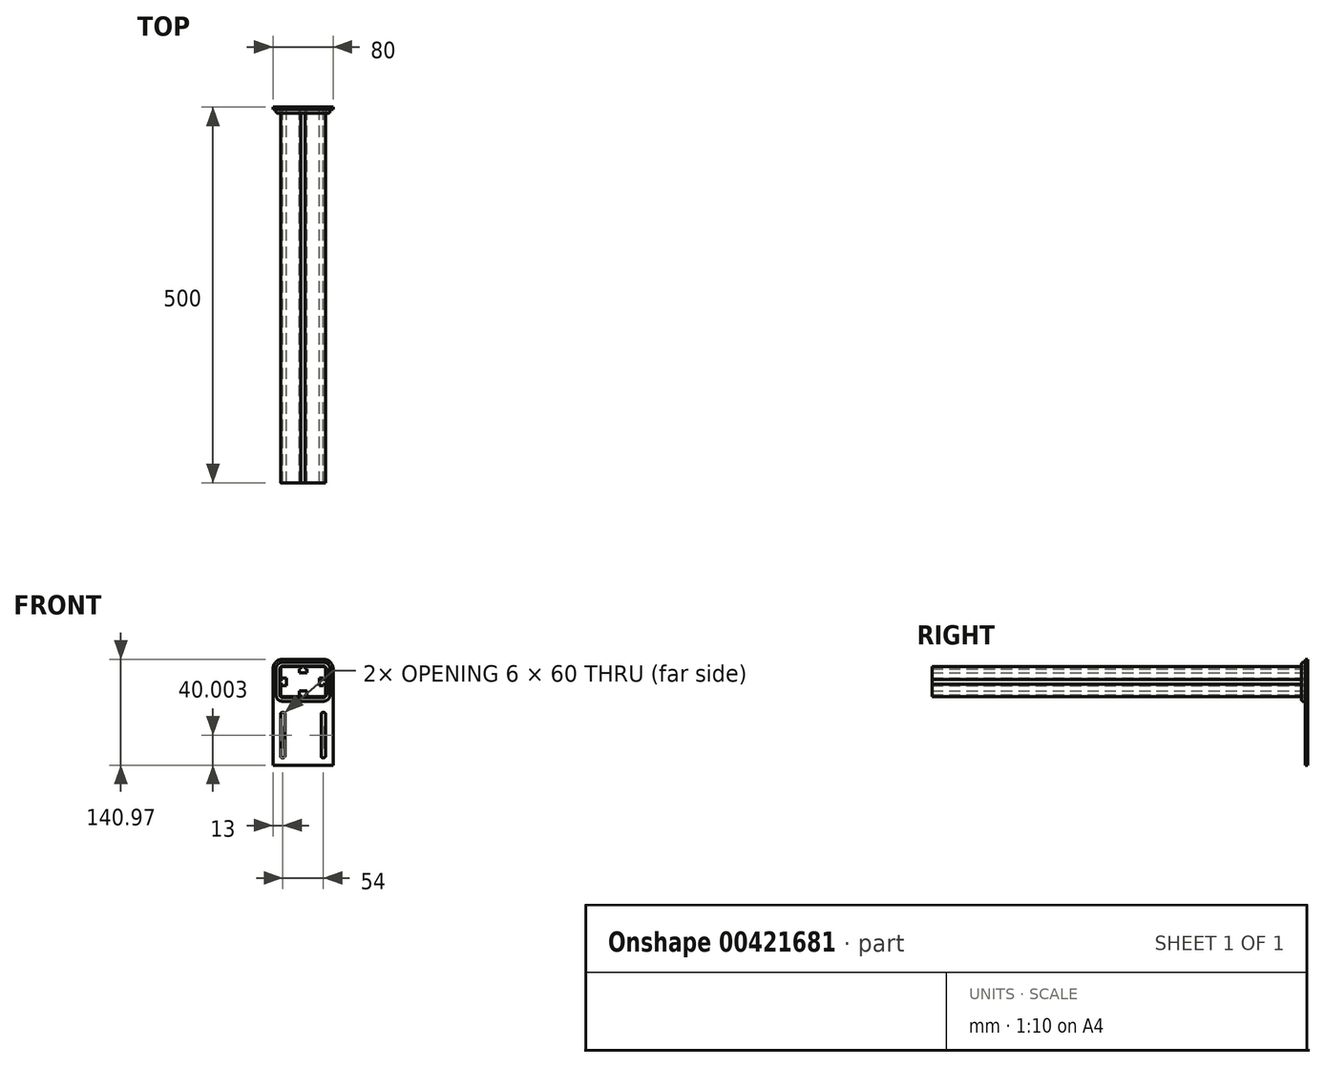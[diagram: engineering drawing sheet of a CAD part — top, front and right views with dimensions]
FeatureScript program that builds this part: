
annotation { "Feature Type Name" : "Feature", "Feature Type Description" : "" }
export const myFeature = defineFeature(function(context is Context, id is Id, definition is map)
    precondition{}
    {
        {
            var Q0;
            Q0=qCreatedBy(makeId("Front.planeOp"),FACE);
            var sketch = newSketch(context, id + "F0", { "sketchPlane" : qUnion([Q0])});
            skLineSegment(sketch, "E0.bottom", {"start": v(27, -20) * mm, "end": v(3, -20) * mm});
            skLineSegment(sketch, "E0.top", {"start": v(27, 20) * mm, "end": v(3, 20) * mm});
            skLineSegment(sketch, "E0.left", {"start": v(30, -17) * mm, "end": v(30, -3) * mm});
            skLineSegment(sketch, "E0.right", {"start": v(-30, -17) * mm, "end": v(-30, -3) * mm});
            skPoint(sketch, "E0.middle", {"position": v(0, 0) * mm});
            skPoint(sketch, "E1.visualSharp", {"position": v(-30, 20) * mm});
            skArc(sketch, "E1.filletArc", {"start": v(-27, 20) * mm, "mid": v(-29.12, 19.12) * mm, "end": v(-30, 17) * mm});
            skPoint(sketch, "E2.visualSharp", {"position": v(-30, -20) * mm});
            skArc(sketch, "E2.filletArc", {"start": v(-30, -17) * mm, "mid": v(-29.12, -19.12) * mm, "end": v(-27, -20) * mm});
            skPoint(sketch, "E3.visualSharp", {"position": v(30, -20) * mm});
            skArc(sketch, "E3.filletArc", {"start": v(27, -20) * mm, "mid": v(29.12, -19.12) * mm, "end": v(30, -17) * mm});
            skPoint(sketch, "E4.visualSharp", {"position": v(30, 20) * mm});
            skArc(sketch, "E4.filletArc", {"start": v(30, 17) * mm, "mid": v(29.12, 19.12) * mm, "end": v(27, 20) * mm});
            skLineSegment(sketch, "E5.bottom", {"start": v(5, 12) * mm, "end": v(-5, 12) * mm});
            skLineSegment(sketch, "E5.top", {"start": v(5, 17) * mm, "end": v(3, 17) * mm});
            skLineSegment(sketch, "E5.left", {"start": v(5, 12) * mm, "end": v(5, 17) * mm});
            skLineSegment(sketch, "E5.right", {"start": v(-5, 12) * mm, "end": v(-5, 17) * mm});
            skPoint(sketch, "E5.middle", {"position": v(0, 14.5) * mm});
            skLineSegment(sketch, "E6", {"start": v(-3, 17) * mm, "end": v(-3, 20) * mm});
            skLineSegment(sketch, "E7.MirrorCS", {"start": v(3, 17) * mm, "end": v(3, 20) * mm});
            skLineSegment(sketch, "E8.trimOffspring", {"start": v(-3, 20) * mm, "end": v(-27, 20) * mm});
            skLineSegment(sketch, "E9.trimOffspring", {"start": v(-3, 17) * mm, "end": v(-5, 17) * mm});
            skLineSegment(sketch, "E10.MirrorCS", {"start": v(-5, -12) * mm, "end": v(-5, -17) * mm});
            skLineSegment(sketch, "E11.MirrorCS", {"start": v(-3, -17) * mm, "end": v(-3, -20) * mm});
            skLineSegment(sketch, "E12.MirrorCS", {"start": v(3, -17) * mm, "end": v(3, -20) * mm});
            skLineSegment(sketch, "E13.MirrorCS", {"start": v(5, -12) * mm, "end": v(5, -17) * mm});
            skLineSegment(sketch, "E14.MirrorCS", {"start": v(5, -17) * mm, "end": v(3, -17) * mm});
            skLineSegment(sketch, "E15.MirrorCS", {"start": v(-3, -17) * mm, "end": v(-5, -17) * mm});
            skLineSegment(sketch, "E16.MirrorCS", {"start": v(5, -12) * mm, "end": v(-5, -12) * mm});
            skLineSegment(sketch, "E17.trimOffspring", {"start": v(-3, -20) * mm, "end": v(-27, -20) * mm});
            skLineSegment(sketch, "E18.bottom", {"start": v(-22, -5) * mm, "end": v(-27, -5) * mm});
            skLineSegment(sketch, "E18.top", {"start": v(-22, 5) * mm, "end": v(-27, 5) * mm});
            skLineSegment(sketch, "E18.left", {"start": v(-22, -5) * mm, "end": v(-22, 5) * mm});
            skLineSegment(sketch, "E18.right", {"start": v(-27, -5) * mm, "end": v(-27, -3) * mm});
            skPoint(sketch, "E18.middle", {"position": v(-24.5, 0) * mm});
            skLineSegment(sketch, "E19", {"start": v(-27, -3) * mm, "end": v(-30, -3) * mm});
            skLineSegment(sketch, "E20.MirrorCS", {"start": v(-27, 3) * mm, "end": v(-30, 3) * mm});
            skLineSegment(sketch, "E21.trimOffspring", {"start": v(-30, 3) * mm, "end": v(-30, 17) * mm});
            skLineSegment(sketch, "E22.trimOffspring", {"start": v(-27, 3) * mm, "end": v(-27, 5) * mm});
            skLineSegment(sketch, "E23.MirrorCS", {"start": v(22, 5) * mm, "end": v(27, 5) * mm});
            skLineSegment(sketch, "E24.MirrorCS", {"start": v(22, -5) * mm, "end": v(22, 5) * mm});
            skLineSegment(sketch, "E25.MirrorCS", {"start": v(22, -5) * mm, "end": v(27, -5) * mm});
            skLineSegment(sketch, "E26.MirrorCS", {"start": v(27, -3) * mm, "end": v(30, -3) * mm});
            skLineSegment(sketch, "E27.MirrorCS", {"start": v(27, 3) * mm, "end": v(30, 3) * mm});
            skLineSegment(sketch, "E28.MirrorCS", {"start": v(27, 3) * mm, "end": v(27, 5) * mm});
            skLineSegment(sketch, "E29.MirrorCS", {"start": v(27, -5) * mm, "end": v(27, -3) * mm});
            skLineSegment(sketch, "E30.trimOffspring", {"start": v(30, 3) * mm, "end": v(30, 17) * mm});
            skSolve(sketch);
        }
        {
            var Q0;
            Q0=makeQuery(id+"F0.imprint","IMPRINT",FACE,{"disambiguationData":[TD([[makeQuery(id+"F0.imprint","IMPRINT",EDGE,{"derivedFrom":sQuery(id+"F0.wireOp",EDGE,"E0.bottom")}),-1.0]])]});
            extrude(context, id + "F1", {"entities" : qUnion([Q0]), "depth" : 500 * mm, "offsetDistance" : 25 * mm});
        }
        {
            var Q0;
            Q0=qCreatedBy(makeId("Front.planeOp"),FACE);
            var sketch = newSketch(context, id + "F2", { "sketchPlane" : qUnion([Q0])});
            skLineSegment(sketch, "E31.0", {"start": v(-3, 30) * mm, "end": v(-27, 30) * mm});
            skArc(sketch, "E31.1", {"start": v(-27, 30) * mm, "mid": v(-36.2, 26.2) * mm, "end": v(-40, 17) * mm});
            skLineSegment(sketch, "E31.2", {"start": v(-40, 3) * mm, "end": v(-40, 17) * mm});
            skLineSegment(sketch, "E32.0", {"start": v(27, 30) * mm, "end": v(3, 30) * mm});
            skArc(sketch, "E32.1", {"start": v(40, 17) * mm, "mid": v(36.2, 26.2) * mm, "end": v(27, 30) * mm});
            skLineSegment(sketch, "E32.2", {"start": v(40, 3) * mm, "end": v(40, 17) * mm});
            skLineSegment(sketch, "E33", {"start": v(-3, 30) * mm, "end": v(3, 30) * mm});
            skLineSegment(sketch, "E34", {"start": v(-40, 3) * mm, "end": v(-40, -110.97) * mm});
            skLineSegment(sketch, "E35", {"start": v(-40, -110.97) * mm, "end": v(40, -110.97) * mm});
            skLineSegment(sketch, "E36", {"start": v(40, -110.97) * mm, "end": v(40, 3) * mm});
            skLineSegment(sketch, "E37.bottom", {"start": v(-26, -100.97) * mm, "end": v(-28, -100.97) * mm});
            skLineSegment(sketch, "E37.top", {"start": v(-26, -40.97) * mm, "end": v(-28, -40.97) * mm});
            skLineSegment(sketch, "E37.left", {"start": v(-24, -98.97) * mm, "end": v(-24, -42.97) * mm});
            skLineSegment(sketch, "E37.right", {"start": v(-30, -98.97) * mm, "end": v(-30, -42.97) * mm});
            skPoint(sketch, "E37.middle", {"position": v(-27, -70.97) * mm});
            skPoint(sketch, "E38.visualSharp", {"position": v(-30, -40.97) * mm});
            skArc(sketch, "E38.filletArc", {"start": v(-28, -40.97) * mm, "mid": v(-29.41, -41.55) * mm, "end": v(-30, -42.97) * mm});
            skPoint(sketch, "E39.visualSharp", {"position": v(-24, -40.97) * mm});
            skArc(sketch, "E39.filletArc", {"start": v(-24, -42.97) * mm, "mid": v(-24.59, -41.55) * mm, "end": v(-26, -40.97) * mm});
            skPoint(sketch, "E40.visualSharp", {"position": v(-30, -100.97) * mm});
            skArc(sketch, "E40.filletArc", {"start": v(-30, -98.97) * mm, "mid": v(-29.41, -100.38) * mm, "end": v(-28, -100.97) * mm});
            skPoint(sketch, "E41.visualSharp", {"position": v(-24, -100.97) * mm});
            skArc(sketch, "E41.filletArc", {"start": v(-26, -100.97) * mm, "mid": v(-24.59, -100.38) * mm, "end": v(-24, -98.97) * mm});
            skLineSegment(sketch, "E42.MirrorCS", {"start": v(24, -98.97) * mm, "end": v(24, -42.97) * mm});
            skLineSegment(sketch, "E43.MirrorCS", {"start": v(30, -98.97) * mm, "end": v(30, -42.97) * mm});
            skLineSegment(sketch, "E44.MirrorCS", {"start": v(26, -40.97) * mm, "end": v(28, -40.97) * mm});
            skArc(sketch, "E45.MirrorCS", {"start": v(24, -42.97) * mm, "mid": v(24.59, -41.55) * mm, "end": v(26, -40.97) * mm});
            skArc(sketch, "E46.MirrorCS", {"start": v(28, -40.97) * mm, "mid": v(29.41, -41.55) * mm, "end": v(30, -42.97) * mm});
            skArc(sketch, "E47.MirrorCS", {"start": v(30, -98.97) * mm, "mid": v(29.41, -100.38) * mm, "end": v(28, -100.97) * mm});
            skLineSegment(sketch, "E48.MirrorCS", {"start": v(26, -100.97) * mm, "end": v(28, -100.97) * mm});
            skArc(sketch, "E49.MirrorCS", {"start": v(26, -100.97) * mm, "mid": v(24.59, -100.38) * mm, "end": v(24, -98.97) * mm});
            skSolve(sketch);
        }
        {
            var Q0;
            Q0=makeQuery(id+"F2.imprint","IMPRINT",FACE,{"disambiguationData":[TD([[makeQuery(id+"F2.imprint","IMPRINT",EDGE,{"derivedFrom":sQuery(id+"F2.wireOp",EDGE,"E31.0")}),1.0]])]});
            extrude(context, id + "F3", {"entities" : qUnion([Q0]), "depth" : 3 * mm, "offsetDistance" : 25 * mm});
        }
        {
            var Q0;
            Q0=makeQuery(id+"F3.opExtrude","CAP_FACE",FACE,{"disambiguationData":[OSD([sQuery(id+"F2.wireOp",EDGE,"E31.0"),sQuery(id+"F2.wireOp",EDGE,"E31.1"),sQuery(id+"F2.wireOp",EDGE,"E31.2"),sQuery(id+"F2.wireOp",EDGE,"E32.0"),sQuery(id+"F2.wireOp",EDGE,"E32.1"),sQuery(id+"F2.wireOp",EDGE,"E32.2"),sQuery(id+"F2.wireOp",EDGE,"E33"),sQuery(id+"F2.wireOp",EDGE,"E34"),sQuery(id+"F2.wireOp",EDGE,"E35"),sQuery(id+"F2.wireOp",EDGE,"E36"),sQuery(id+"F2.wireOp",EDGE,"E37.bottom"),sQuery(id+"F2.wireOp",EDGE,"E37.top"),sQuery(id+"F2.wireOp",EDGE,"E37.left"),sQuery(id+"F2.wireOp",EDGE,"E37.right"),sQuery(id+"F2.wireOp",EDGE,"E38.filletArc"),sQuery(id+"F2.wireOp",EDGE,"E39.filletArc"),sQuery(id+"F2.wireOp",EDGE,"E40.filletArc"),sQuery(id+"F2.wireOp",EDGE,"E41.filletArc"),sQuery(id+"F2.wireOp",EDGE,"E42.MirrorCS"),sQuery(id+"F2.wireOp",EDGE,"E43.MirrorCS"),sQuery(id+"F2.wireOp",EDGE,"E44.MirrorCS"),sQuery(id+"F2.wireOp",EDGE,"E45.MirrorCS"),sQuery(id+"F2.wireOp",EDGE,"E46.MirrorCS"),sQuery(id+"F2.wireOp",EDGE,"E47.MirrorCS"),sQuery(id+"F2.wireOp",EDGE,"E48.MirrorCS"),sQuery(id+"F2.wireOp",EDGE,"E49.MirrorCS")])],"isStart":false});
            var sketch = newSketch(context, id + "F4", { "sketchPlane" : qUnion([Q0])});
            skLineSegment(sketch, "E50.0", {"start": v(-31, 3) * mm, "end": v(-31, 17) * mm});
            skArc(sketch, "E50.1", {"start": v(-27, 21) * mm, "mid": v(-29.83, 19.83) * mm, "end": v(-31, 17) * mm});
            skLineSegment(sketch, "E50.2", {"start": v(-3, 21) * mm, "end": v(-27, 21) * mm});
            skLineSegment(sketch, "E51.0", {"start": v(27, 21) * mm, "end": v(3, 21) * mm});
            skArc(sketch, "E51.1", {"start": v(31, 17) * mm, "mid": v(29.83, 19.83) * mm, "end": v(27, 21) * mm});
            skLineSegment(sketch, "E51.2", {"start": v(31, 3) * mm, "end": v(31, 17) * mm});
            skLineSegment(sketch, "E52.0", {"start": v(-10.74, -81.71) * mm, "end": v(10.74, -81.71) * mm});
            skLineSegment(sketch, "E53.0", {"start": v(-31, -17) * mm, "end": v(-31, -3) * mm});
            skArc(sketch, "E53.1", {"start": v(-31, -17) * mm, "mid": v(-29.83, -19.83) * mm, "end": v(-27, -21) * mm});
            skLineSegment(sketch, "E53.2", {"start": v(-3, -21) * mm, "end": v(-27, -21) * mm});
            skLineSegment(sketch, "E54.0", {"start": v(27, -21) * mm, "end": v(3, -21) * mm});
            skArc(sketch, "E54.1", {"start": v(27, -21) * mm, "mid": v(29.83, -19.83) * mm, "end": v(31, -17) * mm});
            skLineSegment(sketch, "E54.2", {"start": v(31, -17) * mm, "end": v(31, -3) * mm});
            skLineSegment(sketch, "E55.0", {"start": v(-17.05, -88.02) * mm, "end": v(17.05, -88.02) * mm});
            skLineSegment(sketch, "E56", {"start": v(-31, 3) * mm, "end": v(-31, -3) * mm});
            skLineSegment(sketch, "E57", {"start": v(-3, -21) * mm, "end": v(3, -21) * mm});
            skLineSegment(sketch, "E58", {"start": v(31, -3) * mm, "end": v(31, 3) * mm});
            skLineSegment(sketch, "E59", {"start": v(-3, 21) * mm, "end": v(3, 21) * mm});
            skLineSegment(sketch, "E60.0", {"start": v(-3, 26) * mm, "end": v(3, 26) * mm});
            skLineSegment(sketch, "E60.1", {"start": v(27, 26) * mm, "end": v(3, 26) * mm});
            skArc(sketch, "E60.2", {"start": v(36, 17) * mm, "mid": v(33.36, 23.36) * mm, "end": v(27, 26) * mm});
            skLineSegment(sketch, "E60.3", {"start": v(36, 3) * mm, "end": v(36, 17) * mm});
            skLineSegment(sketch, "E60.4", {"start": v(36, -3) * mm, "end": v(36, 3) * mm});
            skLineSegment(sketch, "E60.5", {"start": v(-36, -17) * mm, "end": v(-36, -3) * mm});
            skLineSegment(sketch, "E60.6", {"start": v(-36, 3) * mm, "end": v(-36, -3) * mm});
            skLineSegment(sketch, "E60.7", {"start": v(-36, 3) * mm, "end": v(-36, 17) * mm});
            skArc(sketch, "E60.8", {"start": v(-27, 26) * mm, "mid": v(-33.36, 23.36) * mm, "end": v(-36, 17) * mm});
            skArc(sketch, "E60.9", {"start": v(-36, -17) * mm, "mid": v(-33.36, -23.36) * mm, "end": v(-27, -26) * mm});
            skLineSegment(sketch, "E60.10", {"start": v(-3, -26) * mm, "end": v(-27, -26) * mm});
            skLineSegment(sketch, "E60.11", {"start": v(-3, -26) * mm, "end": v(3, -26) * mm});
            skLineSegment(sketch, "E60.12", {"start": v(27, -26) * mm, "end": v(3, -26) * mm});
            skArc(sketch, "E60.13", {"start": v(27, -26) * mm, "mid": v(33.36, -23.36) * mm, "end": v(36, -17) * mm});
            skLineSegment(sketch, "E60.14", {"start": v(-3, 26) * mm, "end": v(-27, 26) * mm});
            skLineSegment(sketch, "E60.15", {"start": v(36, -17) * mm, "end": v(36, -3) * mm});
            skSolve(sketch);
        }
        {
            var Q0;
            Q0=makeQuery(id+"F4.imprint","IMPRINT",FACE,{"disambiguationData":[TD([[makeQuery(id+"F4.imprint","IMPRINT",EDGE,{"derivedFrom":sQuery(id+"F4.wireOp",EDGE,"E50.0")}),1.0]])]});
            extrude(context, id + "F5", {"entities" : qUnion([Q0]), "operationType" : NewBodyOperationType.ADD, "depth" : 5 * mm, "offsetDistance" : 25 * mm});
        }
        {
            var Q0;
            Q0=makeQuery(id+"F5.opExtrude","CAP_EDGE",EDGE,{"disambiguationData":[OSD([sQuery(id+"F4.wireOp",EDGE,"E60.13")])],"isStart":false});
            fillet(context, id + "F6", {"entities" : qUnion([Q0]), "radius" : 2 * mm, "tangentPropagation" : true, "allowEdgeOverflow" : false});
        }
    });
